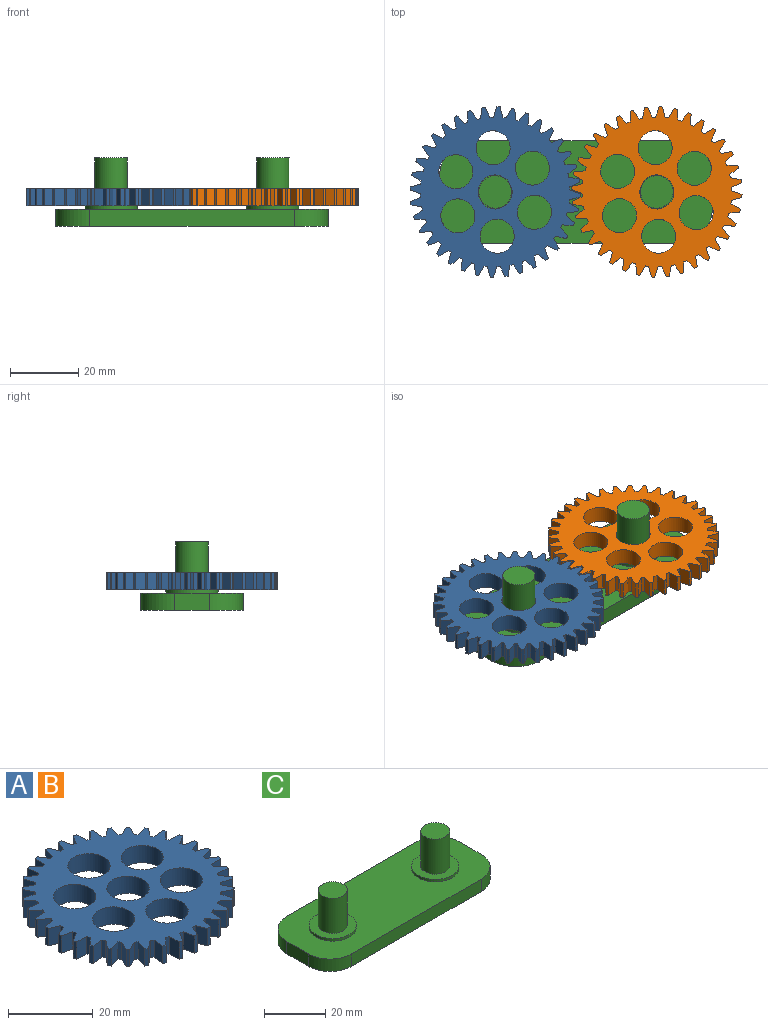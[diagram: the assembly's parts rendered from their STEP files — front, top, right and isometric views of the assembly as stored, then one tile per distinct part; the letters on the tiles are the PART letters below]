
ASSEMBLY  parts=3 mates=2
PART A: 153 faces, bbox 49.9x49.9x5 mm
  f0: cylinder r=5mm len=10mm, axis (0,0,-1), area 157.1mm2, adj f5,f7
  f1: cylinder r=5mm len=10mm, axis (0,0,-1), area 157.1mm2, adj f5,f7
  f2: cylinder r=5mm len=10mm, axis (0,0,-1), area 157.1mm2, adj f5,f7
  f3: cylinder r=5mm len=10mm, axis (0,0,-1), area 157.1mm2, adj f5,f7
  f4: cylinder r=5mm len=10mm, axis (0,0,-1), area 157.1mm2, adj f5,f7
  f5: plane 49.88x49.88mm, normal (0,0,1), area 1173.4mm2, adj f0,f1,f2,f3,f4,f6,f8,f9
  f6: cylinder r=25mm len=5mm, axis (0,0,-1), area 4.6mm2, adj f5,f7,f45,f152
  f7: plane 49.88x49.88mm, normal (0,0,-1), area 1173.4mm2, adj f0,f1,f2,f3,f4,f6,f8,f9
  f8: cylinder r=25mm len=5mm, axis (0,0,-1), area 4.6mm2, adj f5,f7,f149,f150
  f9: cylinder r=25mm len=5mm, axis (0,0,-1), area 4.6mm2, adj f5,f7,f146,f147
  f10: cylinder r=25mm len=5mm, axis (0,0,-1), area 4.6mm2, adj f5,f7,f143,f144
  f11: cylinder r=25mm len=5mm, axis (0,0,-1), area 4.6mm2, adj f5,f7,f140,f141
  f12: cylinder r=25mm len=5mm, axis (0,0,-1), area 4.6mm2, adj f5,f7,f137,f138
  f13: cylinder r=25mm len=5mm, axis (0,0,-1), area 4.6mm2, adj f5,f7,f134,f135
  f14: cylinder r=25mm len=5mm, axis (0,0,-1), area 4.6mm2, adj f5,f7,f131,f132
  f15: cylinder r=25mm len=5mm, axis (0,0,-1), area 4.6mm2, adj f5,f7,f128,f129
  f16: cylinder r=25mm len=5mm, axis (0,0,-1), area 4.6mm2, adj f5,f7,f125,f126
  f17: cylinder r=25mm len=5mm, axis (0,0,-1), area 4.6mm2, adj f5,f7,f122,f123
  f18: cylinder r=25mm len=5mm, axis (0,0,-1), area 4.6mm2, adj f5,f7,f119,f120
  f19: cylinder r=25mm len=5mm, axis (0,0,-1), area 4.6mm2, adj f5,f7,f116,f117
  f20: cylinder r=25mm len=5mm, axis (0,0,-1), area 4.6mm2, adj f5,f7,f113,f114
  f21: cylinder r=25mm len=5mm, axis (0,0,-1), area 4.6mm2, adj f5,f7,f110,f111
  f22: cylinder r=25mm len=5mm, axis (0,0,-1), area 4.6mm2, adj f5,f7,f107,f108
  f23: cylinder r=25mm len=5mm, axis (0,0,-1), area 4.6mm2, adj f5,f7,f104,f105
  f24: cylinder r=25mm len=5mm, axis (0,0,-1), area 4.6mm2, adj f5,f7,f101,f102
  f25: cylinder r=25mm len=5mm, axis (0,0,-1), area 4.6mm2, adj f5,f7,f98,f99
  f26: cylinder r=25mm len=5mm, axis (0,0,-1), area 4.6mm2, adj f5,f7,f95,f96
  f27: cylinder r=25mm len=5mm, axis (0,0,-1), area 4.6mm2, adj f5,f7,f92,f93
  f28: cylinder r=25mm len=5mm, axis (0,0,-1), area 4.6mm2, adj f5,f7,f89,f90
  f29: cylinder r=25mm len=5mm, axis (0,0,-1), area 4.6mm2, adj f5,f7,f86,f87
  f30: cylinder r=25mm len=5mm, axis (0,0,-1), area 4.6mm2, adj f5,f7,f83,f84
  f31: cylinder r=25mm len=5mm, axis (0,0,-1), area 4.6mm2, adj f5,f7,f80,f81
  f32: cylinder r=25mm len=5mm, axis (0,0,-1), area 4.6mm2, adj f5,f7,f77,f78
  f33: cylinder r=25mm len=5mm, axis (0,0,-1), area 4.6mm2, adj f5,f7,f74,f75
  f34: cylinder r=25mm len=5mm, axis (0,0,-1), area 4.6mm2, adj f5,f7,f71,f72
  f35: cylinder r=25mm len=5mm, axis (0,0,-1), area 4.6mm2, adj f5,f7,f68,f69
  f36: cylinder r=25mm len=5mm, axis (0,0,-1), area 4.6mm2, adj f5,f7,f65,f66
  f37: cylinder r=25mm len=5mm, axis (0,0,-1), area 4.6mm2, adj f5,f7,f62,f63
  f38: cylinder r=25mm len=5mm, axis (0,0,-1), area 4.6mm2, adj f5,f7,f59,f60
  f39: cylinder r=25mm len=5mm, axis (0,0,-1), area 4.6mm2, adj f5,f7,f56,f57
  f40: cylinder r=25mm len=5mm, axis (0,0,-1), area 4.6mm2, adj f5,f7,f53,f54
  f41: cylinder r=25mm len=5mm, axis (0,0,-1), area 4.6mm2, adj f5,f7,f50,f51
  f42: cylinder r=5mm len=10mm, axis (0,0,-1), area 157.1mm2, adj f5,f7
  f43: cylinder r=5mm len=10mm, axis (0,0,-1), area 157.1mm2, adj f5,f7
  f44: cylinder r=25mm len=5mm, axis (0,0,-1), area 4.6mm2, adj f5,f7,f47,f48
  f45: plane 5x2.95mm, normal (0.92,0.38,0), area 15.9mm2, adj f5,f6,f7,f46
  f46: cylinder r=22mm len=5mm, axis (0,0,-1), area 5mm2, adj f5,f7,f45,f47
  f47: plane 5x2.95mm, normal (-0.92,0.38,0), area 15.9mm2, adj f5,f7,f44,f46
  f48: plane 5x3.11mm, normal (0.98,0.22,0), area 15.9mm2, adj f5,f7,f44,f49
  f49: cylinder r=22mm len=5mm, axis (0,0,-1), area 5mm2, adj f5,f7,f48,f50
  f50: plane 5x2.69mm, normal (-0.84,0.54,0), area 15.9mm2, adj f5,f7,f41,f49
  f51: plane 5x3.19mm, normal (1,0.04,0), area 15.9mm2, adj f5,f7,f41,f52
  f52: cylinder r=22mm len=5mm, axis (0,0,-1), area 5mm2, adj f5,f7,f51,f53
  f53: plane 5x2.35mm, normal (-0.74,0.68,0), area 15.9mm2, adj f5,f7,f40,f52
  f54: plane 5x3.16mm, normal (0.99,-0.13,0), area 15.9mm2, adj f5,f7,f40,f55
  f55: cylinder r=22mm len=5mm, axis (0,0,-1), area 5mm2, adj f5,f7,f54,f56
  f56: plane 5x2.53mm, normal (-0.61,0.79,0), area 15.9mm2, adj f5,f7,f39,f55
  f57: plane 5x3.04mm, normal (0.95,-0.3,0), area 15.9mm2, adj f5,f7,f39,f58
  f58: cylinder r=22mm len=5mm, axis (0,0,-1), area 5mm2, adj f5,f7,f57,f59
  f59: plane 5x2.83mm, normal (-0.46,0.89,0), area 15.9mm2, adj f5,f7,f38,f58
  f60: plane 5x2.83mm, normal (0.89,-0.46,0), area 15.9mm2, adj f5,f7,f38,f61
  f61: cylinder r=22mm len=5mm, axis (0,0,-1), area 5mm2, adj f5,f7,f60,f62
  f62: plane 5x3.04mm, normal (-0.3,0.95,0), area 15.9mm2, adj f5,f7,f37,f61
  f63: plane 5x2.53mm, normal (0.79,-0.61,0), area 15.9mm2, adj f5,f7,f37,f64
  f64: cylinder r=22mm len=5mm, axis (0,0,-1), area 5mm2, adj f5,f7,f63,f65
  f65: plane 5x3.16mm, normal (-0.13,0.99,0), area 15.9mm2, adj f5,f7,f36,f64
  f66: plane 5x2.35mm, normal (0.68,-0.74,0), area 15.9mm2, adj f5,f7,f36,f67
  f67: cylinder r=22mm len=5mm, axis (0,0,-1), area 5mm2, adj f5,f7,f66,f68
  f68: plane 5x3.19mm, normal (0.04,1,0), area 15.9mm2, adj f5,f7,f35,f67
  f69: plane 5x2.69mm, normal (0.54,-0.84,0), area 15.9mm2, adj f5,f7,f35,f70
  f70: cylinder r=22mm len=5mm, axis (0,0,-1), area 5mm2, adj f5,f7,f69,f71
  f71: plane 5x3.11mm, normal (0.22,0.98,0), area 15.9mm2, adj f5,f7,f34,f70
  f72: plane 5x2.95mm, normal (0.38,-0.92,0), area 15.9mm2, adj f5,f7,f34,f73
  f73: cylinder r=22mm len=5mm, axis (0,0,-1), area 5mm2, adj f5,f7,f72,f74
  f74: plane 5x2.95mm, normal (0.38,0.92,0), area 15.9mm2, adj f5,f7,f33,f73
  f75: plane 5x3.11mm, normal (0.22,-0.98,0), area 15.9mm2, adj f5,f7,f33,f76
  f76: cylinder r=22mm len=5mm, axis (0,0,-1), area 5mm2, adj f5,f7,f75,f77
  f77: plane 5x2.69mm, normal (0.54,0.84,0), area 15.9mm2, adj f5,f7,f32,f76
  f78: plane 5x3.19mm, normal (0.04,-1,0), area 15.9mm2, adj f5,f7,f32,f79
  f79: cylinder r=22mm len=5mm, axis (0,0,-1), area 5mm2, adj f5,f7,f78,f80
  f80: plane 5x2.35mm, normal (0.68,0.74,0), area 15.9mm2, adj f5,f7,f31,f79
  f81: plane 5x3.16mm, normal (-0.13,-0.99,0), area 15.9mm2, adj f5,f7,f31,f82
  f82: cylinder r=22mm len=5mm, axis (0,0,-1), area 5mm2, adj f5,f7,f81,f83
  f83: plane 5x2.53mm, normal (0.79,0.61,0), area 15.9mm2, adj f5,f7,f30,f82
  f84: plane 5x3.04mm, normal (-0.3,-0.95,0), area 15.9mm2, adj f5,f7,f30,f85
  f85: cylinder r=22mm len=5mm, axis (0,0,-1), area 5mm2, adj f5,f7,f84,f86
  f86: plane 5x2.83mm, normal (0.89,0.46,0), area 15.9mm2, adj f5,f7,f29,f85
  f87: plane 5x2.83mm, normal (-0.46,-0.89,0), area 15.9mm2, adj f5,f7,f29,f88
  f88: cylinder r=22mm len=5mm, axis (0,0,-1), area 5mm2, adj f5,f7,f87,f89
  f89: plane 5x3.04mm, normal (0.95,0.3,0), area 15.9mm2, adj f5,f7,f28,f88
  f90: plane 5x2.53mm, normal (-0.61,-0.79,0), area 15.9mm2, adj f5,f7,f28,f91
  f91: cylinder r=22mm len=5mm, axis (0,0,-1), area 5mm2, adj f5,f7,f90,f92
  f92: plane 5x3.16mm, normal (0.99,0.13,0), area 15.9mm2, adj f5,f7,f27,f91
  f93: plane 5x2.35mm, normal (-0.74,-0.68,0), area 15.9mm2, adj f5,f7,f27,f94
  f94: cylinder r=22mm len=5mm, axis (0,0,-1), area 5mm2, adj f5,f7,f93,f95
  f95: plane 5x3.19mm, normal (1,-0.04,0), area 15.9mm2, adj f5,f7,f26,f94
  f96: plane 5x2.69mm, normal (-0.84,-0.54,0), area 15.9mm2, adj f5,f7,f26,f97
  f97: cylinder r=22mm len=5mm, axis (0,0,-1), area 5mm2, adj f5,f7,f96,f98
  f98: plane 5x3.11mm, normal (0.98,-0.22,0), area 15.9mm2, adj f5,f7,f25,f97
  f99: plane 5x2.95mm, normal (-0.92,-0.38,0), area 15.9mm2, adj f5,f7,f25,f100
  f100: cylinder r=22mm len=5mm, axis (0,0,-1), area 5mm2, adj f5,f7,f99,f101
  f101: plane 5x2.95mm, normal (0.92,-0.38,0), area 15.9mm2, adj f5,f7,f24,f100
  f102: plane 5x3.11mm, normal (-0.98,-0.22,0), area 15.9mm2, adj f5,f7,f24,f103
  f103: cylinder r=22mm len=5mm, axis (0,0,-1), area 5mm2, adj f5,f7,f102,f104
  f104: plane 5x2.69mm, normal (0.84,-0.54,0), area 15.9mm2, adj f5,f7,f23,f103
  f105: plane 5x3.19mm, normal (-1,-0.04,0), area 15.9mm2, adj f5,f7,f23,f106
  f106: cylinder r=22mm len=5mm, axis (0,0,-1), area 5mm2, adj f5,f7,f105,f107
  f107: plane 5x2.35mm, normal (0.74,-0.68,0), area 15.9mm2, adj f5,f7,f22,f106
  f108: plane 5x3.16mm, normal (-0.99,0.13,0), area 15.9mm2, adj f5,f7,f22,f109
  f109: cylinder r=22mm len=5mm, axis (0,0,-1), area 5mm2, adj f5,f7,f108,f110
  f110: plane 5x2.53mm, normal (0.61,-0.79,0), area 15.9mm2, adj f5,f7,f21,f109
  f111: plane 5x3.04mm, normal (-0.95,0.3,0), area 15.9mm2, adj f5,f7,f21,f112
  f112: cylinder r=22mm len=5mm, axis (0,0,-1), area 5mm2, adj f5,f7,f111,f113
  f113: plane 5x2.83mm, normal (0.46,-0.89,0), area 15.9mm2, adj f5,f7,f20,f112
  f114: plane 5x2.83mm, normal (-0.89,0.46,0), area 15.9mm2, adj f5,f7,f20,f115
  f115: cylinder r=22mm len=5mm, axis (0,0,-1), area 5mm2, adj f5,f7,f114,f116
  f116: plane 5x3.04mm, normal (0.3,-0.95,0), area 15.9mm2, adj f5,f7,f19,f115
  f117: plane 5x2.53mm, normal (-0.79,0.61,0), area 15.9mm2, adj f5,f7,f19,f118
  f118: cylinder r=22mm len=5mm, axis (0,0,-1), area 5mm2, adj f5,f7,f117,f119
  f119: plane 5x3.16mm, normal (0.13,-0.99,0), area 15.9mm2, adj f5,f7,f18,f118
  f120: plane 5x2.35mm, normal (-0.68,0.74,0), area 15.9mm2, adj f5,f7,f18,f121
  f121: cylinder r=22mm len=5mm, axis (0,0,-1), area 5mm2, adj f5,f7,f120,f122
  f122: plane 5x3.19mm, normal (-0.04,-1,0), area 15.9mm2, adj f5,f7,f17,f121
  f123: plane 5x2.69mm, normal (-0.54,0.84,0), area 15.9mm2, adj f5,f7,f17,f124
  f124: cylinder r=22mm len=5mm, axis (0,0,-1), area 5mm2, adj f5,f7,f123,f125
  f125: plane 5x3.11mm, normal (-0.22,-0.98,0), area 15.9mm2, adj f5,f7,f16,f124
  f126: plane 5x2.95mm, normal (-0.38,0.92,0), area 15.9mm2, adj f5,f7,f16,f127
  f127: cylinder r=22mm len=5mm, axis (0,0,-1), area 5mm2, adj f5,f7,f126,f128
  f128: plane 5x2.95mm, normal (-0.38,-0.92,0), area 15.9mm2, adj f5,f7,f15,f127
  f129: plane 5x3.11mm, normal (-0.22,0.98,0), area 15.9mm2, adj f5,f7,f15,f130
  f130: cylinder r=22mm len=5mm, axis (0,0,-1), area 5mm2, adj f5,f7,f129,f131
  f131: plane 5x2.69mm, normal (-0.54,-0.84,0), area 15.9mm2, adj f5,f7,f14,f130
  f132: plane 5x3.19mm, normal (-0.04,1,0), area 15.9mm2, adj f5,f7,f14,f133
  f133: cylinder r=22mm len=5mm, axis (0,0,-1), area 5mm2, adj f5,f7,f132,f134
  f134: plane 5x2.35mm, normal (-0.68,-0.74,0), area 15.9mm2, adj f5,f7,f13,f133
  f135: plane 5x3.16mm, normal (0.13,0.99,0), area 15.9mm2, adj f5,f7,f13,f136
  f136: cylinder r=22mm len=5mm, axis (0,0,-1), area 5mm2, adj f5,f7,f135,f137
  f137: plane 5x2.53mm, normal (-0.79,-0.61,0), area 15.9mm2, adj f5,f7,f12,f136
  f138: plane 5x3.04mm, normal (0.3,0.95,0), area 15.9mm2, adj f5,f7,f12,f139
  f139: cylinder r=22mm len=5mm, axis (0,0,-1), area 5mm2, adj f5,f7,f138,f140
  f140: plane 5x2.83mm, normal (-0.89,-0.46,0), area 15.9mm2, adj f5,f7,f11,f139
  f141: plane 5x2.83mm, normal (0.46,0.89,0), area 15.9mm2, adj f5,f7,f11,f142
  f142: cylinder r=22mm len=5mm, axis (0,0,-1), area 5mm2, adj f5,f7,f141,f143
  f143: plane 5x3.04mm, normal (-0.95,-0.3,0), area 15.9mm2, adj f5,f7,f10,f142
  f144: plane 5x2.53mm, normal (0.61,0.79,0), area 15.9mm2, adj f5,f7,f10,f145
  f145: cylinder r=22mm len=5mm, axis (0,0,-1), area 5mm2, adj f5,f7,f144,f146
  f146: plane 5x3.16mm, normal (-0.99,-0.13,0), area 15.9mm2, adj f5,f7,f9,f145
  f147: plane 5x2.35mm, normal (0.74,0.68,0), area 15.9mm2, adj f5,f7,f9,f148
  f148: cylinder r=22mm len=5mm, axis (0,0,-1), area 5mm2, adj f5,f7,f147,f149
  f149: plane 5x3.19mm, normal (-1,0.04,0), area 15.9mm2, adj f5,f7,f8,f148
  f150: plane 5x2.69mm, normal (0.84,0.54,0), area 15.9mm2, adj f5,f7,f8,f151
  f151: cylinder r=22mm len=5mm, axis (0,0,-1), area 5mm2, adj f5,f7,f150,f152
  f152: plane 5x3.11mm, normal (-0.98,0.22,0), area 15.9mm2, adj f5,f6,f7,f151
PART B: same geometry as A
PART C: 18 faces, bbox 80x30x20 mm
  f0: cylinder r=10mm len=10mm, axis (0,0,-1), area 78.5mm2, adj f1,f7,f8,f9
  f1: plane 60x5mm, normal (0,-1,0), area 300mm2, adj f0,f2,f8,f9
  f2: cylinder r=10mm len=10mm, axis (0,0,-1), area 78.5mm2, adj f1,f3,f8,f9
  f3: plane 10x5mm, normal (1,0,0), area 50mm2, adj f2,f4,f8,f9
  f4: cylinder r=10mm len=10mm, axis (0,0,-1), area 78.5mm2, adj f3,f5,f8,f9
  f5: plane 60x5mm, normal (0,1,0), area 300mm2, adj f4,f6,f8,f9
  f6: cylinder r=10mm len=10mm, axis (0,0,-1), area 78.5mm2, adj f5,f7,f8,f9
  f7: plane 10x5mm, normal (-1,0,0), area 50mm2, adj f0,f6,f8,f9
  f8: plane 80x30mm, normal (0,0,1), area 1936.8mm2, adj f0,f1,f2,f3,f4,f5,f6,f7
  f9: plane 80x30mm, normal (0,0,-1), area 2314.2mm2, adj f0,f1,f2,f3,f4,f5,f6,f7
  f10: cylinder r=7.75mm len=15.5mm, axis (0,0,-1), area 48.7mm2, adj f8,f11
  f11: plane 15.5x15.5mm, normal (0,0,1), area 117.8mm2, adj f10,f14
  f12: cylinder r=7.75mm len=15.5mm, axis (0,0,-1), area 48.7mm2, adj f8,f13
  f13: plane 15.5x15.5mm, normal (0,0,1), area 117.8mm2, adj f12,f16
  f14: cylinder r=4.75mm len=14mm, axis (0,0,-1), area 417.8mm2, adj f11,f15
  f15: plane 9.5x9.5mm, normal (0,0,1), area 70.9mm2, adj f14
  f16: cylinder r=4.75mm len=14mm, axis (0,0,-1), area 417.8mm2, adj f13,f17
  f17: plane 9.5x9.5mm, normal (0,0,1), area 70.9mm2, adj f16
PLACE A rot(axis=(0,0,1),2.7deg) t=(16.25,-15,6)mm
PLACE B rot(axis=(0,0,1),2.3deg) t=(63.75,-15,6)mm
PLACE C at identity fixed
MATE revolute B.f6 <-> C.f12  axis (0,0,-1) through (63.75,-15,6)mm
MATE revolute A.f6 <-> C.f10  axis (0,0,-1) through (16.25,-15,6)mm
